# Revit family: FS1910-FL
name_source: partatom
category: Plumbing Fixtures
revit_build: Autodesk Revit 2018 (Build: 20170223_1515(x64)
units: mm (PartAtom-declared; Revit-internal decimal feet)

## family parameters
Cut with Voids When Loaded = No
Host = Face
Part Type = Normal
Room Calculation Point = No
Round Connector Dimension = Use Radius
Shared = No

## types (3) — shared parameters
Default Elevation = 0' - 0"
Description = 12” X 12” X 4” STAINLESS STEEL FLOOR AREA & INDIRECT SANITARY WASTE DRAIN WITH FLANGE
Floor Drain Material = Paint - Sherwin Williams Paint - #952C2A - Bellwood Red
Manufacturer = MIFAB
URL = WWW.MIFAB.COM
zero-valued in all types: CWFU, WFU

## per-type parameters (varying)
| type | Model | Pipe Diameter | Pipe Radius |
| FS1912-FL_2" | FS1912-FL | 0' - 2" | 0' - 1" |
| FS1913-FL_3" | FS1913-FL | 0' - 3" | 0' - 1 1/2" |
| FS1914-FL_4" | FS1914-FL | 0' - 4" | 0' - 2" |

## geometry (parser evidence)
native form markers: Blend x2, Sweep x6
no freeform markers — native parametric forms only
